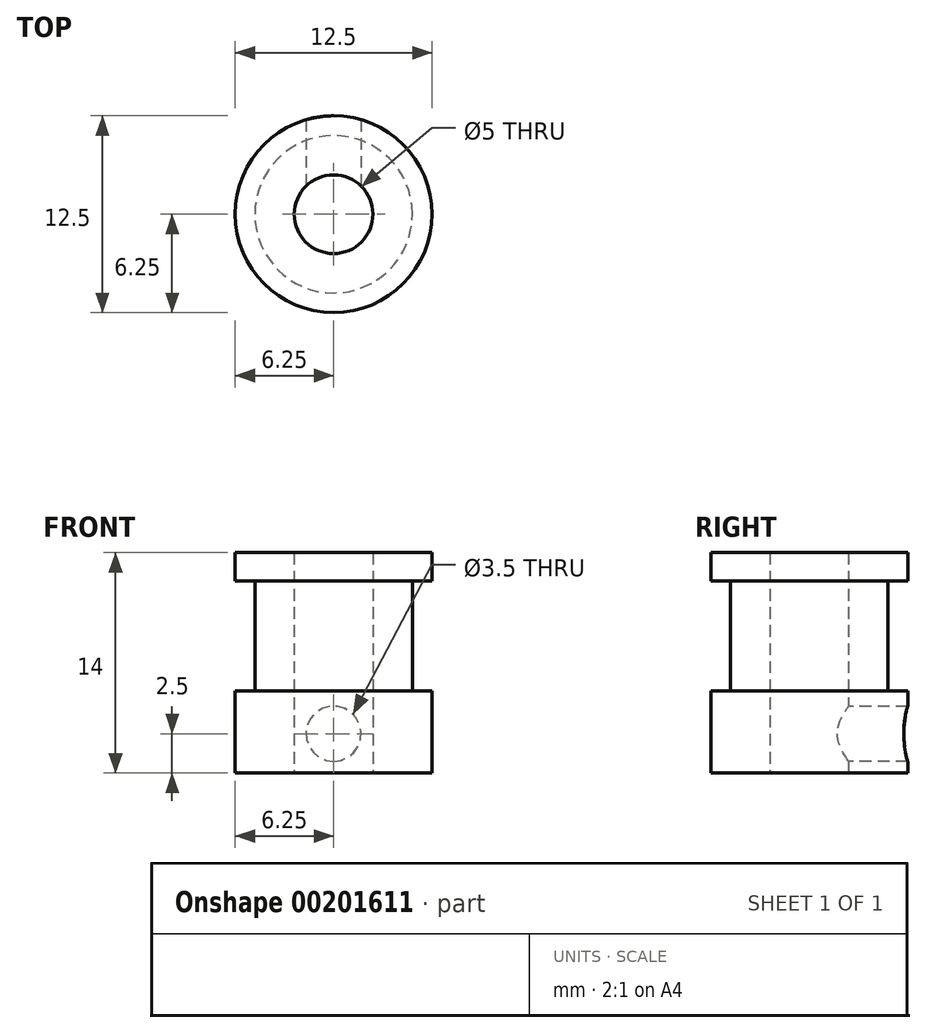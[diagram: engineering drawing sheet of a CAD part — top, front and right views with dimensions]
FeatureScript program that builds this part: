
annotation { "Feature Type Name" : "Feature", "Feature Type Description" : "" }
export const myFeature = defineFeature(function(context is Context, id is Id, definition is map)
    precondition{}
    {
        {
            var Q0;
            Q0=qCreatedBy(makeId("Top.planeOp"),FACE);
            var sketch = newSketch(context, id + "F0", { "sketchPlane" : qUnion([Q0])});
            skCircle(sketch, "E0", {"center": v(0, 0) * mm, "radius": 6.25 * mm});
            skCircle(sketch, "E1", {"center": v(0, 0) * mm, "radius": 2.5 * mm});
            skSolve(sketch);
        }
        {
            var Q0;
            Q0=makeQuery(id+"F0.imprint","IMPRINT",FACE,{"disambiguationData":[TD([[makeQuery(id+"F0.imprint","IMPRINT",EDGE,{"derivedFrom":sQuery(id+"F0.wireOp",EDGE,"E0")}),1.0]])]});
            extrude(context, id + "F1", {"entities" : qUnion([Q0]), "depth" : 14 * mm});
        }
        {
            var Q0;
            Q0=qCreatedBy(makeId("Front.planeOp"),FACE);
            var sketch = newSketch(context, id + "F2", { "sketchPlane" : qUnion([Q0])});
            skLineSegment(sketch, "E2.bottom", {"start": v(-8.73, 12.22) * mm, "end": v(-5, 12.22) * mm});
            skLineSegment(sketch, "E2.top", {"start": v(-8.73, 5.22) * mm, "end": v(-5, 5.22) * mm});
            skLineSegment(sketch, "E2.left", {"start": v(-8.73, 12.22) * mm, "end": v(-8.73, 5.22) * mm});
            skLineSegment(sketch, "E2.right", {"start": v(-5, 12.22) * mm, "end": v(-5, 5.22) * mm});
            skLineSegment(sketch, "E3", {"start": v(0, 20.32) * mm, "end": v(0, -5.85) * mm, "construction": true});
            skSolve(sketch);
        }
        {
            var Q0;
            Q0=makeQuery(id+"F2.imprint","IMPRINT",FACE,{"disambiguationData":[TD([[makeQuery(id+"F2.imprint","IMPRINT",EDGE,{"derivedFrom":sQuery(id+"F2.wireOp",EDGE,"E2.bottom")}),-1.0]])]});
            var Q1;
            Q1=sQuery(id+"F2.wireOp",EDGE,"E3");
            revolve(context, id + "F3", {"operationType" : NewBodyOperationType.REMOVE, "entities" : qUnion([Q0]), "axis" : qUnion([Q1]), "revolveType" : RevolveType.FULL, "oppositeDirection" : true});
        }
        {
            var Q0;
            Q0=qCreatedBy(makeId("Front.planeOp"),FACE);
            var sketch = newSketch(context, id + "F4", { "sketchPlane" : qUnion([Q0])});
            skCircle(sketch, "E4", {"center": v(0, 2.5) * mm, "radius": 1.75 * mm});
            skSolve(sketch);
        }
        {
            var Q0;
            Q0=makeQuery(id+"F4.imprint","IMPRINT",FACE,{"disambiguationData":[TD([[makeQuery(id+"F4.imprint","IMPRINT",EDGE,{"derivedFrom":sQuery(id+"F4.wireOp",EDGE,"E4")}),1.0]])]});
            extrude(context, id + "F5", {"entities" : qUnion([Q0]), "operationType" : NewBodyOperationType.REMOVE, "oppositeDirection" : true, "depth" : 25 * mm});
        }
    });
